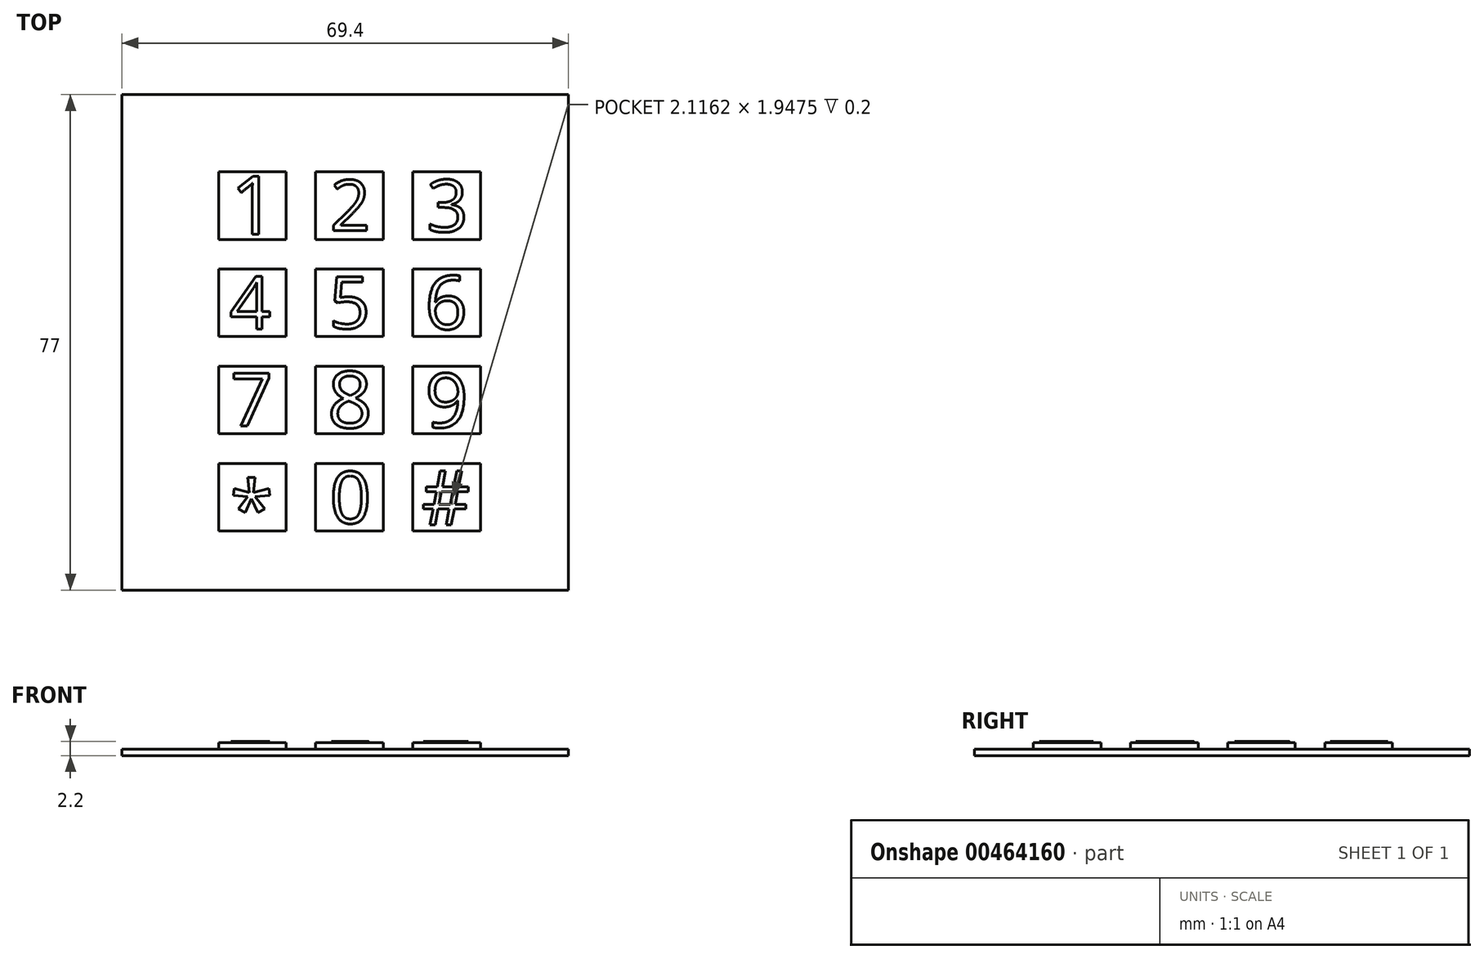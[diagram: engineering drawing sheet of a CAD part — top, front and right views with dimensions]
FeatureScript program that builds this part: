
annotation { "Feature Type Name" : "Feature", "Feature Type Description" : "" }
export const myFeature = defineFeature(function(context is Context, id is Id, definition is map)
    precondition{}
    {
        {
            var Q0;
            Q0=qCreatedBy(makeId("Top.planeOp"),FACE);
            var sketch = newSketch(context, id + "F0", { "sketchPlane" : qUnion([Q0])});
            skLineSegment(sketch, "E0.bottom", {"start": v(-34.26, 43.25) * mm, "end": v(35.14, 43.25) * mm});
            skLineSegment(sketch, "E0.top", {"start": v(-34.26, -33.75) * mm, "end": v(35.14, -33.75) * mm});
            skLineSegment(sketch, "E0.left", {"start": v(-34.26, 43.25) * mm, "end": v(-34.26, -33.75) * mm});
            skLineSegment(sketch, "E0.right", {"start": v(35.14, 43.25) * mm, "end": v(35.14, -33.75) * mm});
            skSolve(sketch);
        }
        {
            var Q0;
            Q0 = qSketchRegion(id + "F0", true);
            extrude(context, id + "F1", {"entities" : qUnion([Q0]), "depth" : 1 * mm});
        }
        {
            var Q0;
            Q0=makeQuery(id+"F1.opExtrude","CAP_FACE",FACE,{"disambiguationData":[OSD([sQuery(id+"F0.wireOp",EDGE,"E0.bottom"),sQuery(id+"F0.wireOp",EDGE,"E0.top"),sQuery(id+"F0.wireOp",EDGE,"E0.left"),sQuery(id+"F0.wireOp",EDGE,"E0.right")])],"isStart":false});
            var sketch = newSketch(context, id + "F2", { "sketchPlane" : qUnion([Q0])});
            skLineSegment(sketch, "E1.bottom", {"start": v(-19.26, 31.25) * mm, "end": v(-8.76, 31.25) * mm});
            skLineSegment(sketch, "E1.top", {"start": v(-19.26, 20.75) * mm, "end": v(-8.76, 20.75) * mm});
            skLineSegment(sketch, "E1.left", {"start": v(-19.26, 31.25) * mm, "end": v(-19.26, 20.75) * mm});
            skLineSegment(sketch, "E1.right", {"start": v(-8.76, 31.25) * mm, "end": v(-8.76, 20.75) * mm});
            skLineSegment(sketch, "E2.0.1.0", {"start": v(-8.76, 16.15) * mm, "end": v(-8.76, 5.65) * mm});
            skLineSegment(sketch, "E2.0.1.1", {"start": v(-19.26, 16.15) * mm, "end": v(-19.26, 5.65) * mm});
            skLineSegment(sketch, "E2.0.1.2", {"start": v(-19.26, 5.65) * mm, "end": v(-8.76, 5.65) * mm});
            skLineSegment(sketch, "E2.0.1.3", {"start": v(-19.26, 16.15) * mm, "end": v(-8.76, 16.15) * mm});
            skLineSegment(sketch, "E2.0.2.0", {"start": v(-8.76, 1.05) * mm, "end": v(-8.76, -9.45) * mm});
            skLineSegment(sketch, "E2.0.2.1", {"start": v(-19.26, 1.05) * mm, "end": v(-19.26, -9.45) * mm});
            skLineSegment(sketch, "E2.0.2.2", {"start": v(-19.26, -9.45) * mm, "end": v(-8.76, -9.45) * mm});
            skLineSegment(sketch, "E2.0.2.3", {"start": v(-19.26, 1.05) * mm, "end": v(-8.76, 1.05) * mm});
            skLineSegment(sketch, "E2.0.3.0", {"start": v(-8.76, -14.05) * mm, "end": v(-8.76, -24.55) * mm});
            skLineSegment(sketch, "E2.0.3.1", {"start": v(-19.26, -14.05) * mm, "end": v(-19.26, -24.55) * mm});
            skLineSegment(sketch, "E2.0.3.2", {"start": v(-19.26, -24.55) * mm, "end": v(-8.76, -24.55) * mm});
            skLineSegment(sketch, "E2.0.3.3", {"start": v(-19.26, -14.05) * mm, "end": v(-8.76, -14.05) * mm});
            skLineSegment(sketch, "E2.1.0.0", {"start": v(6.34, 31.25) * mm, "end": v(6.34, 20.75) * mm});
            skLineSegment(sketch, "E2.1.0.1", {"start": v(-4.16, 31.25) * mm, "end": v(-4.16, 20.75) * mm});
            skLineSegment(sketch, "E2.1.0.2", {"start": v(-4.16, 20.75) * mm, "end": v(6.34, 20.75) * mm});
            skLineSegment(sketch, "E2.1.0.3", {"start": v(-4.16, 31.25) * mm, "end": v(6.34, 31.25) * mm});
            skLineSegment(sketch, "E2.1.1.0", {"start": v(6.34, 16.15) * mm, "end": v(6.34, 5.65) * mm});
            skLineSegment(sketch, "E2.1.1.1", {"start": v(-4.16, 16.15) * mm, "end": v(-4.16, 5.65) * mm});
            skLineSegment(sketch, "E2.1.1.2", {"start": v(-4.16, 5.65) * mm, "end": v(6.34, 5.65) * mm});
            skLineSegment(sketch, "E2.1.1.3", {"start": v(-4.16, 16.15) * mm, "end": v(6.34, 16.15) * mm});
            skLineSegment(sketch, "E2.1.2.0", {"start": v(6.34, 1.05) * mm, "end": v(6.34, -9.45) * mm});
            skLineSegment(sketch, "E2.1.2.1", {"start": v(-4.16, 1.05) * mm, "end": v(-4.16, -9.45) * mm});
            skLineSegment(sketch, "E2.1.2.2", {"start": v(-4.16, -9.45) * mm, "end": v(6.34, -9.45) * mm});
            skLineSegment(sketch, "E2.1.2.3", {"start": v(-4.16, 1.05) * mm, "end": v(6.34, 1.05) * mm});
            skLineSegment(sketch, "E2.1.3.0", {"start": v(6.34, -14.05) * mm, "end": v(6.34, -24.55) * mm});
            skLineSegment(sketch, "E2.1.3.1", {"start": v(-4.16, -14.05) * mm, "end": v(-4.16, -24.55) * mm});
            skLineSegment(sketch, "E2.1.3.2", {"start": v(-4.16, -24.55) * mm, "end": v(6.34, -24.55) * mm});
            skLineSegment(sketch, "E2.1.3.3", {"start": v(-4.16, -14.05) * mm, "end": v(6.34, -14.05) * mm});
            skLineSegment(sketch, "E2.2.0.0", {"start": v(21.44, 31.25) * mm, "end": v(21.44, 20.75) * mm});
            skLineSegment(sketch, "E2.2.0.1", {"start": v(10.94, 31.25) * mm, "end": v(10.94, 20.75) * mm});
            skLineSegment(sketch, "E2.2.0.2", {"start": v(10.94, 20.75) * mm, "end": v(21.44, 20.75) * mm});
            skLineSegment(sketch, "E2.2.0.3", {"start": v(10.94, 31.25) * mm, "end": v(21.44, 31.25) * mm});
            skLineSegment(sketch, "E2.2.1.0", {"start": v(21.44, 16.15) * mm, "end": v(21.44, 5.65) * mm});
            skLineSegment(sketch, "E2.2.1.1", {"start": v(10.94, 16.15) * mm, "end": v(10.94, 5.65) * mm});
            skLineSegment(sketch, "E2.2.1.2", {"start": v(10.94, 5.65) * mm, "end": v(21.44, 5.65) * mm});
            skLineSegment(sketch, "E2.2.1.3", {"start": v(10.94, 16.15) * mm, "end": v(21.44, 16.15) * mm});
            skLineSegment(sketch, "E2.2.2.0", {"start": v(21.44, 1.05) * mm, "end": v(21.44, -9.45) * mm});
            skLineSegment(sketch, "E2.2.2.1", {"start": v(10.94, 1.05) * mm, "end": v(10.94, -9.45) * mm});
            skLineSegment(sketch, "E2.2.2.2", {"start": v(10.94, -9.45) * mm, "end": v(21.44, -9.45) * mm});
            skLineSegment(sketch, "E2.2.2.3", {"start": v(10.94, 1.05) * mm, "end": v(21.44, 1.05) * mm});
            skLineSegment(sketch, "E2.2.3.0", {"start": v(21.44, -14.05) * mm, "end": v(21.44, -24.55) * mm});
            skLineSegment(sketch, "E2.2.3.1", {"start": v(10.94, -14.05) * mm, "end": v(10.94, -24.55) * mm});
            skLineSegment(sketch, "E2.2.3.2", {"start": v(10.94, -24.55) * mm, "end": v(21.44, -24.55) * mm});
            skLineSegment(sketch, "E2.2.3.3", {"start": v(10.94, -14.05) * mm, "end": v(21.44, -14.05) * mm});
            skLineSegment(sketch, "E2.direction1", {"start": v(-19.26, 20.75) * mm, "end": v(-4.16, 20.75) * mm, "construction": true});
            skLineSegment(sketch, "E2.direction2", {"start": v(-19.26, 20.75) * mm, "end": v(-19.26, 5.65) * mm, "construction": true});
            skSolve(sketch);
        }
        {
            var Q0;
            Q0 = qSketchRegion(id + "F2", true);
            var Q1;
            Q1 = qConstructionFilter(qBodyType(qCreatedBy(id + "F2" ,EDGE), BodyType.WIRE), ConstructionObject.NO);
            extrude(context, id + "F3", {"entities" : qUnion([Q0]), "surfaceEntities" : qUnion([Q1]), "depth" : 1 * mm});
        }
        {
            var Q0;
            Q0=makeQuery(id+"F3.opExtrude","CAP_FACE",FACE,{"disambiguationData":[OSD([sQuery(id+"F2.wireOp",EDGE,"E1.bottom"),sQuery(id+"F2.wireOp",EDGE,"E1.top"),sQuery(id+"F2.wireOp",EDGE,"E1.left"),sQuery(id+"F2.wireOp",EDGE,"E1.right")])],"isStart":false});
            var sketch = newSketch(context, id + "F4", { "sketchPlane" : qUnion([Q0])});
            skText(sketch, "E3", { "text": "1", "fontName": "OpenSans-Regular.ttf"});
            const initialGuessF4  = {"E3": [-0.01742, 0.02158, 1, 0, 0.00906]};
            skSetInitialGuess(sketch, initialGuessF4);
            skSolve(sketch);
        }
        {
            var Q0;
            Q0 = qSketchRegion(id + "F4", true);
            extrude(context, id + "F5", {"entities" : qUnion([Q0]), "operationType" : NewBodyOperationType.ADD, "depth" : 0.2 * mm});
        }
        {
            var Q0;
            Q0=makeQuery(id+"F3.opExtrude","CAP_FACE",FACE,{"disambiguationData":[OSD([sQuery(id+"F2.wireOp",EDGE,"E2.1.0.0"),sQuery(id+"F2.wireOp",EDGE,"E2.1.0.1"),sQuery(id+"F2.wireOp",EDGE,"E2.1.0.2"),sQuery(id+"F2.wireOp",EDGE,"E2.1.0.3")])],"isStart":false});
            var sketch = newSketch(context, id + "F6", { "sketchPlane" : qUnion([Q0])});
            skText(sketch, "E4", { "text": "2", "fontName": "OpenSans-Regular.ttf"});
            const initialGuessF6  = {"E4": [-0.0019, 0.02215, 1, 0, 0.00789]};
            skSetInitialGuess(sketch, initialGuessF6);
            skSolve(sketch);
        }
        {
            var Q0;
            Q0 = qSketchRegion(id + "F6", true);
            extrude(context, id + "F7", {"entities" : qUnion([Q0]), "operationType" : NewBodyOperationType.ADD, "depth" : 0.2 * mm});
        }
        {
            var Q0;
            Q0=makeQuery(id+"F3.opExtrude","CAP_FACE",FACE,{"disambiguationData":[OSD([sQuery(id+"F2.wireOp",EDGE,"E2.2.0.0"),sQuery(id+"F2.wireOp",EDGE,"E2.2.0.1"),sQuery(id+"F2.wireOp",EDGE,"E2.2.0.2"),sQuery(id+"F2.wireOp",EDGE,"E2.2.0.3")])],"isStart":false});
            var sketch = newSketch(context, id + "F8", { "sketchPlane" : qUnion([Q0])});
            skText(sketch, "E5", { "text": "3", "fontName": "OpenSans-Regular.ttf"});
            const initialGuessF8  = {"E5": [0.0131, 0.02195, 1, 0, 0.00812]};
            skSetInitialGuess(sketch, initialGuessF8);
            skSolve(sketch);
        }
        {
            var Q0;
            Q0 = qSketchRegion(id + "F8", true);
            extrude(context, id + "F9", {"entities" : qUnion([Q0]), "operationType" : NewBodyOperationType.ADD, "depth" : 0.2 * mm});
        }
        {
            var Q0;
            Q0=makeQuery(id+"F3.opExtrude","CAP_FACE",FACE,{"disambiguationData":[OSD([sQuery(id+"F2.wireOp",EDGE,"E2.0.1.0"),sQuery(id+"F2.wireOp",EDGE,"E2.0.1.1"),sQuery(id+"F2.wireOp",EDGE,"E2.0.1.2"),sQuery(id+"F2.wireOp",EDGE,"E2.0.1.3")])],"isStart":false});
            var sketch = newSketch(context, id + "F10", { "sketchPlane" : qUnion([Q0])});
            skText(sketch, "E6", { "text": "4", "fontName": "OpenSans-Regular.ttf"});
            const initialGuessF10  = {"E6": [-0.01755, 0.00683, 1, 0, 0.0082]};
            skSetInitialGuess(sketch, initialGuessF10);
            skSolve(sketch);
        }
        {
            var Q0;
            Q0 = qSketchRegion(id + "F10", true);
            extrude(context, id + "F11", {"entities" : qUnion([Q0]), "operationType" : NewBodyOperationType.ADD, "depth" : 0.2 * mm});
        }
        {
            var Q0;
            Q0=makeQuery(id+"F3.opExtrude","CAP_FACE",FACE,{"disambiguationData":[OSD([sQuery(id+"F2.wireOp",EDGE,"E2.1.1.0"),sQuery(id+"F2.wireOp",EDGE,"E2.1.1.1"),sQuery(id+"F2.wireOp",EDGE,"E2.1.1.2"),sQuery(id+"F2.wireOp",EDGE,"E2.1.1.3")])],"isStart":false});
            var sketch = newSketch(context, id + "F12", { "sketchPlane" : qUnion([Q0])});
            skText(sketch, "E7", { "text": "5", "fontName": "OpenSans-Regular.ttf"});
            const initialGuessF12  = {"E7": [-0.00212, 0.00692, 1, 0, 0.00812]};
            skSetInitialGuess(sketch, initialGuessF12);
            skSolve(sketch);
        }
        {
            var Q0;
            Q0 = qSketchRegion(id + "F12", true);
            extrude(context, id + "F13", {"entities" : qUnion([Q0]), "operationType" : NewBodyOperationType.ADD, "depth" : 0.2 * mm});
        }
        {
            var Q0;
            Q0=makeQuery(id+"F3.opExtrude","CAP_FACE",FACE,{"disambiguationData":[OSD([sQuery(id+"F2.wireOp",EDGE,"E2.2.1.0"),sQuery(id+"F2.wireOp",EDGE,"E2.2.1.1"),sQuery(id+"F2.wireOp",EDGE,"E2.2.1.2"),sQuery(id+"F2.wireOp",EDGE,"E2.2.1.3")])],"isStart":false});
            var sketch = newSketch(context, id + "F14", { "sketchPlane" : qUnion([Q0])});
            skText(sketch, "E8", { "text": "6", "fontName": "OpenSans-Regular.ttf"});
            const initialGuessF14  = {"E8": [0.01282, 0.00681, 1, 0, 0.00834]};
            skSetInitialGuess(sketch, initialGuessF14);
            skSolve(sketch);
        }
        {
            var Q0;
            Q0 = qSketchRegion(id + "F14", true);
            extrude(context, id + "F15", {"entities" : qUnion([Q0]), "operationType" : NewBodyOperationType.ADD, "depth" : 0.2 * mm});
        }
        {
            var Q0;
            Q0=makeQuery(id+"F3.opExtrude","CAP_FACE",FACE,{"disambiguationData":[OSD([sQuery(id+"F2.wireOp",EDGE,"E2.0.2.0"),sQuery(id+"F2.wireOp",EDGE,"E2.0.2.1"),sQuery(id+"F2.wireOp",EDGE,"E2.0.2.2"),sQuery(id+"F2.wireOp",EDGE,"E2.0.2.3")])],"isStart":false});
            var sketch = newSketch(context, id + "F16", { "sketchPlane" : qUnion([Q0])});
            skText(sketch, "E9", { "text": "7", "fontName": "OpenSans-Regular.ttf"});
            const initialGuessF16  = {"E9": [-0.0174, -0.00826, 1, 0, 0.00826]};
            skSetInitialGuess(sketch, initialGuessF16);
            skSolve(sketch);
        }
        {
            var Q0;
            Q0 = qSketchRegion(id + "F16", true);
            extrude(context, id + "F17", {"entities" : qUnion([Q0]), "operationType" : NewBodyOperationType.ADD, "depth" : 0.2 * mm});
        }
        {
            var Q0;
            Q0=makeQuery(id+"F3.opExtrude","CAP_FACE",FACE,{"disambiguationData":[OSD([sQuery(id+"F2.wireOp",EDGE,"E2.1.2.0"),sQuery(id+"F2.wireOp",EDGE,"E2.1.2.1"),sQuery(id+"F2.wireOp",EDGE,"E2.1.2.2"),sQuery(id+"F2.wireOp",EDGE,"E2.1.2.3")])],"isStart":false});
            var sketch = newSketch(context, id + "F18", { "sketchPlane" : qUnion([Q0])});
            skText(sketch, "E10", { "text": "8", "fontName": "OpenSans-Regular.ttf"});
            const initialGuessF18  = {"E10": [-0.00232, -0.0085, 1, 0, 0.00878]};
            skSetInitialGuess(sketch, initialGuessF18);
            skSolve(sketch);
        }
        {
            var Q0;
            Q0 = qSketchRegion(id + "F18", true);
            extrude(context, id + "F19", {"entities" : qUnion([Q0]), "operationType" : NewBodyOperationType.ADD, "depth" : 0.2 * mm});
        }
        {
            var Q0;
            Q0=makeQuery(id+"F3.opExtrude","CAP_FACE",FACE,{"disambiguationData":[OSD([sQuery(id+"F2.wireOp",EDGE,"E2.2.2.0"),sQuery(id+"F2.wireOp",EDGE,"E2.2.2.1"),sQuery(id+"F2.wireOp",EDGE,"E2.2.2.2"),sQuery(id+"F2.wireOp",EDGE,"E2.2.2.3")])],"isStart":false});
            var sketch = newSketch(context, id + "F20", { "sketchPlane" : qUnion([Q0])});
            skText(sketch, "E11", { "text": "9", "fontName": "OpenSans-Regular.ttf"});
            const initialGuessF20  = {"E11": [0.01284, -0.00845, 1, 0, 0.00845]};
            skSetInitialGuess(sketch, initialGuessF20);
            skSolve(sketch);
        }
        {
            var Q0;
            Q0 = qSketchRegion(id + "F20", true);
            extrude(context, id + "F21", {"entities" : qUnion([Q0]), "operationType" : NewBodyOperationType.ADD, "depth" : 0.2 * mm});
        }
        {
            var Q0;
            Q0=makeQuery(id+"F3.opExtrude","CAP_FACE",FACE,{"disambiguationData":[OSD([sQuery(id+"F2.wireOp",EDGE,"E2.0.3.0"),sQuery(id+"F2.wireOp",EDGE,"E2.0.3.1"),sQuery(id+"F2.wireOp",EDGE,"E2.0.3.2"),sQuery(id+"F2.wireOp",EDGE,"E2.0.3.3")])],"isStart":false});
            var sketch = newSketch(context, id + "F22", { "sketchPlane" : qUnion([Q0])});
            skText(sketch, "E12", { "text": "*", "fontName": "OpenSans-Regular.ttf"});
            const initialGuessF22  = {"E12": [-0.01748, -0.0255, 1, 0, 0.00879]};
            skSetInitialGuess(sketch, initialGuessF22);
            skSolve(sketch);
        }
        {
            var Q0;
            Q0 = qSketchRegion(id + "F22", true);
            extrude(context, id + "F23", {"entities" : qUnion([Q0]), "operationType" : NewBodyOperationType.ADD, "depth" : 0.2 * mm});
        }
        {
            var Q0;
            Q0=makeQuery(id+"F3.opExtrude","CAP_FACE",FACE,{"disambiguationData":[OSD([sQuery(id+"F2.wireOp",EDGE,"E2.1.3.0"),sQuery(id+"F2.wireOp",EDGE,"E2.1.3.1"),sQuery(id+"F2.wireOp",EDGE,"E2.1.3.2"),sQuery(id+"F2.wireOp",EDGE,"E2.1.3.3")])],"isStart":false});
            var sketch = newSketch(context, id + "F24", { "sketchPlane" : qUnion([Q0])});
            skText(sketch, "E13", { "text": "0", "fontName": "OpenSans-Regular.ttf"});
            const initialGuessF24  = {"E13": [-0.00197, -0.02336, 1, 0, 0.00808]};
            skSetInitialGuess(sketch, initialGuessF24);
            skSolve(sketch);
        }
        {
            var Q0;
            Q0 = qSketchRegion(id + "F24", true);
            extrude(context, id + "F25", {"entities" : qUnion([Q0]), "operationType" : NewBodyOperationType.ADD, "depth" : 0.2 * mm});
        }
        {
            var Q0;
            Q0=makeQuery(id+"F3.opExtrude","CAP_FACE",FACE,{"disambiguationData":[OSD([sQuery(id+"F2.wireOp",EDGE,"E2.2.3.0"),sQuery(id+"F2.wireOp",EDGE,"E2.2.3.1"),sQuery(id+"F2.wireOp",EDGE,"E2.2.3.2"),sQuery(id+"F2.wireOp",EDGE,"E2.2.3.3")])],"isStart":false});
            var sketch = newSketch(context, id + "F26", { "sketchPlane" : qUnion([Q0])});
            skText(sketch, "E14", { "text": "#", "fontName": "OpenSans-Regular.ttf"});
            const initialGuessF26  = {"E14": [0.01229, -0.0236, 1, 0, 0.00845]};
            skSetInitialGuess(sketch, initialGuessF26);
            skSolve(sketch);
        }
        {
            var Q0;
            Q0 = qSketchRegion(id + "F26", true);
            extrude(context, id + "F27", {"entities" : qUnion([Q0]), "operationType" : NewBodyOperationType.ADD, "depth" : 0.2 * mm});
        }
    });
